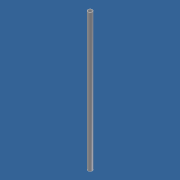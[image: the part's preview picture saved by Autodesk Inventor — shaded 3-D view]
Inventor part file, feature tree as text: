
AUTODESK INVENTOR PART (.ipt)
format: ipt  version: unknown  size: 158,720 bytes
history: native  units: mm
features: extrude x1, sketch x1
ambient origin geometry x8: Origin, YZ Plane, XZ Plane, XY Plane, X Axis, Y Axis, Z Axis, Center Point
bodies: Solido1 (feature_tree)
feature tree (2):
  extrude  "Estrusione1"  Depth=21.0mm
  sketch  "Schizzo1"
